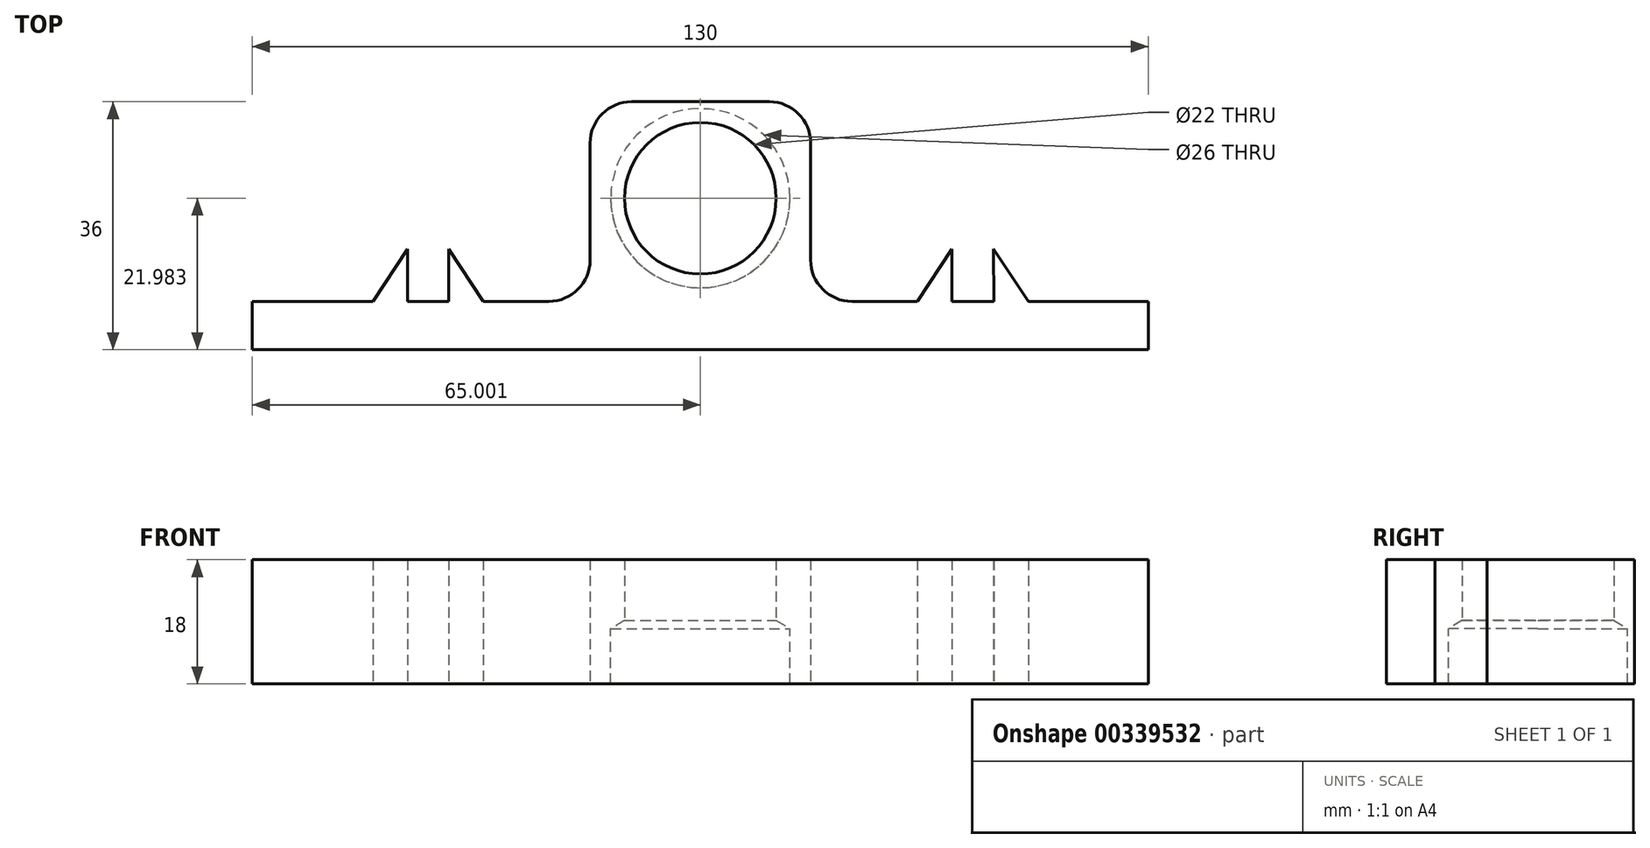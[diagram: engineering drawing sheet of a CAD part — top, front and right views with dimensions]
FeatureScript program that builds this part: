
annotation { "Feature Type Name" : "Feature", "Feature Type Description" : "" }
export const myFeature = defineFeature(function(context is Context, id is Id, definition is map)
    precondition{}
    {
        {
            var Q0;
            Q0=qCreatedBy(makeId("Top.planeOp"),FACE);
            var sketch = newSketch(context, id + "F0", { "sketchPlane" : qUnion([Q0])});
            skLineSegment(sketch, "E0.bottom", {"start": v(-109.57, 51.63) * mm, "end": v(20.43, 51.63) * mm});
            skLineSegment(sketch, "E0.top", {"start": v(-109.57, 15.63) * mm, "end": v(20.43, 15.63) * mm});
            skLineSegment(sketch, "E0.left", {"start": v(-109.57, 51.63) * mm, "end": v(-109.57, 15.63) * mm});
            skLineSegment(sketch, "E0.right", {"start": v(20.43, 51.63) * mm, "end": v(20.43, 15.63) * mm});
            skCircle(sketch, "E1", {"center": v(-84.07, 37.63) * mm, "radius": 8 * mm});
            skCircle(sketch, "E2", {"center": v(-5.07, 37.63) * mm, "radius": 8 * mm});
            skPoint(sketch, "E3.centerSnap0", {"position": v(-44.57, 15.63) * mm});
            skLineSegment(sketch, "E4", {"start": v(-109.57, 22.63) * mm, "end": v(20.43, 22.63) * mm});
            skLineSegment(sketch, "E5", {"start": v(-81.07, 22.63) * mm, "end": v(-81.07, 37.63) * mm});
            skLineSegment(sketch, "E6", {"start": v(-81.07, 37.63) * mm, "end": v(-87.07, 37.63) * mm});
            skLineSegment(sketch, "E7", {"start": v(-87.07, 37.63) * mm, "end": v(-87.07, 22.63) * mm});
            skLineSegment(sketch, "E8", {"start": v(-87.07, 30.22) * mm, "end": v(-92.07, 22.63) * mm});
            skLineSegment(sketch, "E9", {"start": v(-92.07, 22.63) * mm, "end": v(-76.07, 22.63) * mm});
            skLineSegment(sketch, "E10", {"start": v(-76.07, 22.63) * mm, "end": v(-81.07, 30.22) * mm});
            skLineSegment(sketch, "E11", {"start": v(-8.07, 22.63) * mm, "end": v(-8.07, 37.6) * mm});
            skLineSegment(sketch, "E12", {"start": v(-8.07, 37.6) * mm, "end": v(-2.07, 37.63) * mm});
            skLineSegment(sketch, "E13", {"start": v(-2.07, 37.63) * mm, "end": v(-1.97, 22.63) * mm});
            skLineSegment(sketch, "E14", {"start": v(-8.07, 30.22) * mm, "end": v(-13.07, 22.63) * mm});
            skPoint(sketch, "E14.startSnap0", {"position": v(-8.07, 30.11) * mm});
            skLineSegment(sketch, "E15", {"start": v(-13.07, 22.63) * mm, "end": v(3.03, 22.63) * mm});
            skLineSegment(sketch, "E16", {"start": v(3.03, 22.63) * mm, "end": v(-2.02, 30.24) * mm});
            skLineSegment(sketch, "E17", {"start": v(-60.57, 15.63) * mm, "end": v(-60.57, 51.63) * mm});
            skLineSegment(sketch, "E18", {"start": v(-28.57, 15.63) * mm, "end": v(-28.57, 51.63) * mm});
            skLineSegment(sketch, "E19", {"start": v(-44.57, 15.63) * mm, "end": v(-44.57, 51.63) * mm, "construction": true});
            skLineSegment(sketch, "E20", {"start": v(-81.07, 37.63) * mm, "end": v(-8.07, 37.6) * mm, "construction": true});
            skCircle(sketch, "E21", {"center": v(-44.57, 37.61) * mm, "radius": 11 * mm});
            skCircle(sketch, "E22", {"center": v(-44.57, 37.61) * mm, "radius": 13 * mm});
            skSolve(sketch);
        }
        {
            var Q0;
            {var subQ0=sQuery(id+"F0.wireOp",EDGE,"E17");var subQ1=sQuery(id+"F0.wireOp",EDGE,"E0.top");var subQ2=makeQuery(id+"F0.imprint","INTERSECT",VERTEX,{"derivedFrom":[subQ1,subQ0]});Q0=makeQuery(id+"F0.imprint","IMPRINT",FACE,{"disambiguationData":[TD([[makeQuery(id+"F0.imprint","IMPRINT",EDGE,{"disambiguationData":[TD([[subQ2,-1.0]])],"derivedFrom":subQ1}),1.0]])]});}
            var Q1;
            Q1=makeQuery(id+"F0.imprint","IMPRINT",FACE,{"disambiguationData":[TD([[makeQuery(id+"F0.imprint","IMPRINT",EDGE,{"derivedFrom":sQuery(id+"F0.wireOp",EDGE,"E22")}),-1.0]])]});
            var Q2;
            {var subQ7=sQuery(id+"F0.wireOp",EDGE,"E0.left");var subQ10=sQuery(id+"F0.wireOp",EDGE,"E0.top");var subQ11=makeQuery(id+"F0.imprint","INTERSECT",VERTEX,{"derivedFrom":[subQ10,subQ7]});Q2=makeQuery(id+"F0.imprint","IMPRINT",FACE,{"disambiguationData":[TD([[makeQuery(id+"F0.imprint","IMPRINT",EDGE,{"disambiguationData":[TD([[subQ11,-1.0]])],"derivedFrom":subQ10}),1.0]])]});}
            var Q3;
            {var subQ1=sQuery(id+"F0.wireOp",EDGE,"E0.right");var subQ8=sQuery(id+"F0.wireOp",EDGE,"E0.top");var subQ9=makeQuery(id+"F0.imprint","INTERSECT",VERTEX,{"derivedFrom":[subQ8,subQ1]});Q3=makeQuery(id+"F0.imprint","IMPRINT",FACE,{"disambiguationData":[TD([[makeQuery(id+"F0.imprint","IMPRINT",EDGE,{"disambiguationData":[TD([[subQ9,1.0]])],"derivedFrom":subQ8}),1.0]])]});}
            var Q4;
            Q4=makeQuery(id+"F0.imprint","IMPRINT",FACE,{"disambiguationData":[TD([[makeQuery(id+"F0.imprint","IMPRINT",EDGE,{"derivedFrom":sQuery(id+"F0.wireOp",EDGE,"E21")}),-1.0]])]});
            var Q5;
            {var subQ3=sQuery(id+"F0.wireOp",EDGE,"E10");Q5=makeQuery(id+"F0.imprint","IMPRINT",FACE,{"disambiguationData":[TD([[makeQuery(id+"F0.imprint","IMPRINT",EDGE,{"derivedFrom":subQ3}),1.0]])]});}
            var Q6;
            {var subQ3=sQuery(id+"F0.wireOp",EDGE,"E5");var subQ5=sQuery(id+"F0.wireOp",EDGE,"E9");var subQ6=makeQuery(id+"F0.imprint","INTERSECT",VERTEX,{"derivedFrom":[subQ3,subQ5]});Q6=makeQuery(id+"F0.imprint","IMPRINT",FACE,{"disambiguationData":[TD([[makeQuery(id+"F0.imprint","IMPRINT",EDGE,{"disambiguationData":[TD([[subQ6,1.0]])],"derivedFrom":subQ5}),1.0]])]});}
            var Q7;
            {var subQ3=sQuery(id+"F0.wireOp",EDGE,"E8");Q7=makeQuery(id+"F0.imprint","IMPRINT",FACE,{"disambiguationData":[TD([[makeQuery(id+"F0.imprint","IMPRINT",EDGE,{"derivedFrom":subQ3}),1.0]])]});}
            var Q8;
            {var subQ3=sQuery(id+"F0.wireOp",EDGE,"E14");Q8=makeQuery(id+"F0.imprint","IMPRINT",FACE,{"disambiguationData":[TD([[makeQuery(id+"F0.imprint","IMPRINT",EDGE,{"derivedFrom":subQ3}),1.0]])]});}
            var Q9;
            {var subQ0=sQuery(id+"F0.wireOp",EDGE,"E11");var subQ5=sQuery(id+"F0.wireOp",EDGE,"E15");var subQ6=makeQuery(id+"F0.imprint","INTERSECT",VERTEX,{"derivedFrom":[subQ0,subQ5]});Q9=makeQuery(id+"F0.imprint","IMPRINT",FACE,{"disambiguationData":[TD([[makeQuery(id+"F0.imprint","IMPRINT",EDGE,{"disambiguationData":[TD([[subQ6,-1.0]])],"derivedFrom":subQ5}),1.0]])]});}
            var Q10;
            {var subQ3=sQuery(id+"F0.wireOp",EDGE,"E16");Q10=makeQuery(id+"F0.imprint","IMPRINT",FACE,{"disambiguationData":[TD([[makeQuery(id+"F0.imprint","IMPRINT",EDGE,{"derivedFrom":subQ3}),1.0]])]});}
            extrude(context, id + "F1", {"entities" : qUnion([Q0, Q1, Q2, Q3, Q4, Q5, Q6, Q7, Q8, Q9, Q10]), "depth" : 18 * mm});
        }
        {
            var Q0;
            Q0=sQuery(id+"F0.wireOp",VERTEX,"E22.center");
            var Q1;
            Q1=makeQuery(id+"F1.opExtrude","SWEPT_BODY",BODY,{"disambiguationData":[OSD([sQuery(id+"F0.wireOp",EDGE,"E0.bottom"),sQuery(id+"F0.wireOp",EDGE,"E0.top"),sQuery(id+"F0.wireOp",EDGE,"E0.left"),sQuery(id+"F0.wireOp",EDGE,"E0.right"),sQuery(id+"F0.wireOp",EDGE,"E1"),sQuery(id+"F0.wireOp",EDGE,"E2"),sQuery(id+"F0.wireOp",EDGE,"E4"),sQuery(id+"F0.wireOp",EDGE,"E8"),sQuery(id+"F0.wireOp",EDGE,"E10"),sQuery(id+"F0.wireOp",EDGE,"E14"),sQuery(id+"F0.wireOp",EDGE,"E16"),sQuery(id+"F0.wireOp",EDGE,"E17"),sQuery(id+"F0.wireOp",EDGE,"E18"),sQuery(id+"F0.wireOp",EDGE,"E21")])]});
            hole(context, id + "F2", {"style" : HoleStyle.SIMPLE, "endStyle" : HoleEndStyle.BLIND, "oppositeDirection" : true, "holeDiameter" : 26 * mm, "holeDepth" : 8 * mm, "isTappedThrough" : true, "tappedDepth" : 12 * mm, "tapClearance" : 3, "locations" : qUnion([Q0]), "scope" : qUnion([Q1])});
        }
        {
            var Q0;
            Q0=makeQuery(id+"F1.opExtrude","SWEPT_EDGE",EDGE,{"disambiguationData":[OSD([sQuery(id+"F0.wireOp",EDGE,"E4"),sQuery(id+"F0.wireOp",EDGE,"E17")])]});
            var Q1;
            Q1=makeQuery(id+"F1.opExtrude","SWEPT_EDGE",EDGE,{"disambiguationData":[OSD([sQuery(id+"F0.wireOp",EDGE,"E4"),sQuery(id+"F0.wireOp",EDGE,"E18")])]});
            var Q2;
            Q2=makeQuery(id+"F1.opExtrude","SWEPT_EDGE",EDGE,{"disambiguationData":[OSD([sQuery(id+"F0.wireOp",EDGE,"E0.bottom"),sQuery(id+"F0.wireOp",EDGE,"E17")])]});
            var Q3;
            Q3=makeQuery(id+"F1.opExtrude","SWEPT_EDGE",EDGE,{"disambiguationData":[OSD([sQuery(id+"F0.wireOp",EDGE,"E0.bottom"),sQuery(id+"F0.wireOp",EDGE,"E18")])]});
            fillet(context, id + "F3", {"entities" : qUnion([Q0, Q1, Q2, Q3]), "radius" : 6 * mm, "tangentPropagation" : true, "allowEdgeOverflow" : false});
        }
    });
